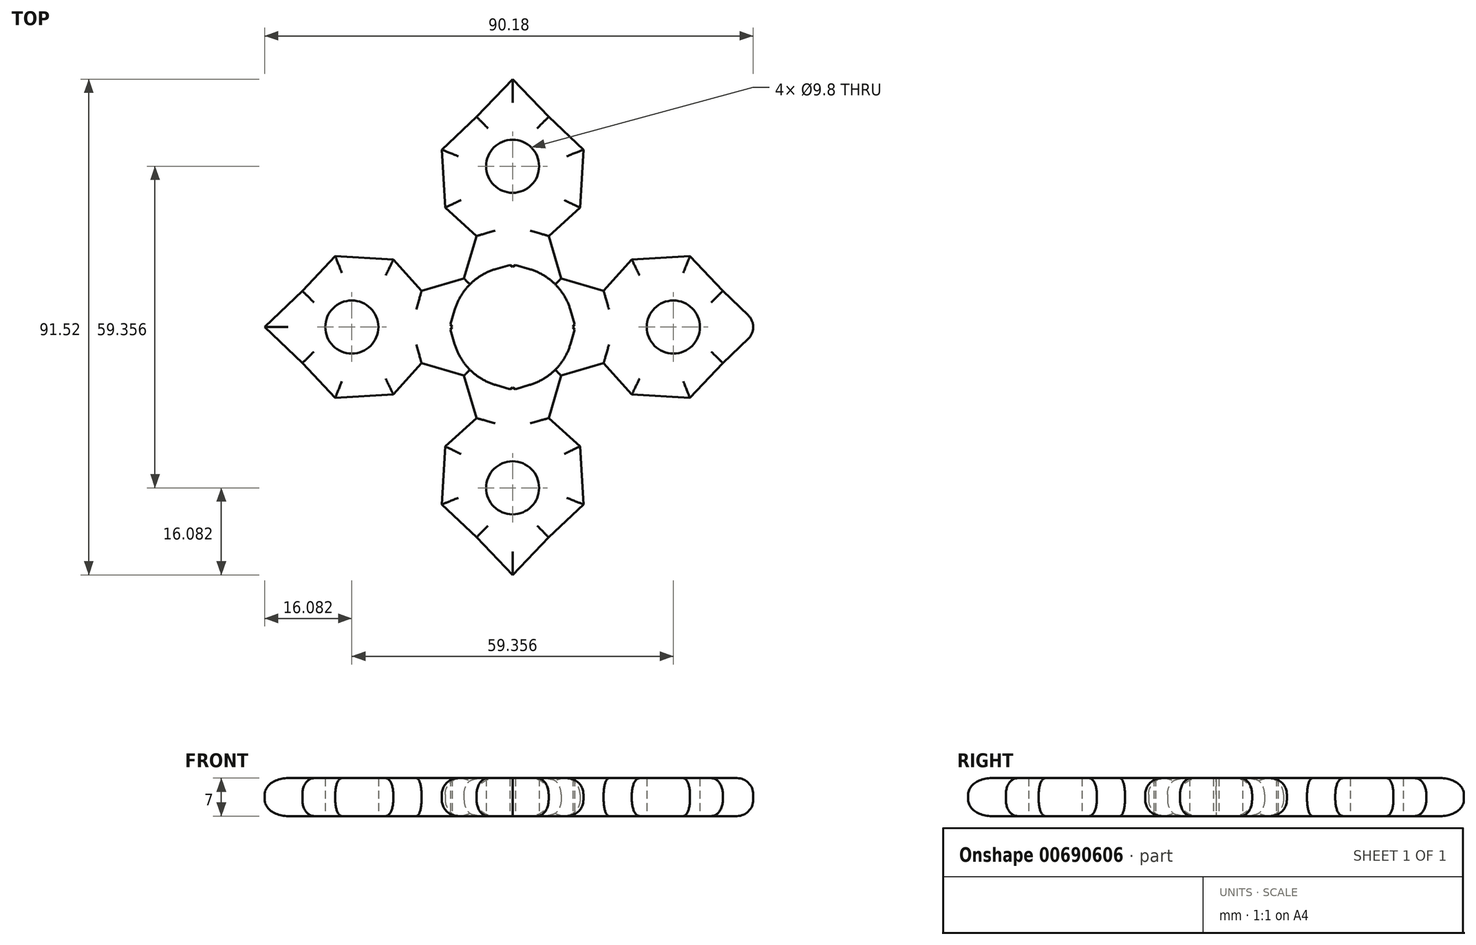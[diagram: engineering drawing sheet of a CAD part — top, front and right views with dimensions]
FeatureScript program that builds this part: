
annotation { "Feature Type Name" : "Feature", "Feature Type Description" : "" }
export const myFeature = defineFeature(function(context is Context, id is Id, definition is map)
    precondition{}
    {
        {
            var Q0;
            Q0=qCreatedBy(makeId("Top.planeOp"),FACE);
            var sketch = newSketch(context, id + "F0", { "sketchPlane" : qUnion([Q0])});
            skCircle(sketch, "E0", {"center": v(0, 0) * mm, "radius": 11.14 * mm});
            skCircle(sketch, "E1", {"center": v(29.68, 0) * mm, "radius": 4.9 * mm});
            skLineSegment(sketch, "E2", {"start": v(0, 11.14) * mm, "end": v(0.51, 11.46) * mm});
            skLineSegment(sketch, "E3", {"start": v(0.51, 11.46) * mm, "end": v(16.8, 6.66) * mm});
            skLineSegment(sketch, "E4", {"start": v(16.8, 6.66) * mm, "end": v(22.02, 12.45) * mm});
            skLineSegment(sketch, "E5", {"start": v(22.02, 12.45) * mm, "end": v(32.74, 13.08) * mm});
            skLineSegment(sketch, "E6", {"start": v(32.74, 13.08) * mm, "end": v(38.81, 6.66) * mm});
            skLineSegment(sketch, "E7", {"start": v(38.81, 6.66) * mm, "end": v(45.76, 0) * mm});
            skLineSegment(sketch, "E8.MirrorCS", {"start": v(0.51, -11.46) * mm, "end": v(16.8, -6.66) * mm});
            skLineSegment(sketch, "E9.MirrorCS", {"start": v(0, -11.14) * mm, "end": v(0.51, -11.46) * mm});
            skLineSegment(sketch, "E10.MirrorCS", {"start": v(16.8, -6.66) * mm, "end": v(22.02, -12.45) * mm});
            skLineSegment(sketch, "E11.MirrorCS", {"start": v(22.02, -12.45) * mm, "end": v(32.74, -13.08) * mm});
            skLineSegment(sketch, "E12.MirrorCS", {"start": v(32.74, -13.08) * mm, "end": v(38.81, -6.66) * mm});
            skLineSegment(sketch, "E13.MirrorCS", {"start": v(38.81, -6.66) * mm, "end": v(45.76, 0) * mm});
            skLineSegment(sketch, "E14.1.0", {"start": v(-12.45, 22.02) * mm, "end": v(-13.08, 32.74) * mm});
            skLineSegment(sketch, "E14.1.1", {"start": v(-13.08, 32.74) * mm, "end": v(-6.66, 38.81) * mm});
            skLineSegment(sketch, "E14.1.2", {"start": v(11.46, 0.51) * mm, "end": v(6.66, 16.8) * mm});
            skLineSegment(sketch, "E14.1.3", {"start": v(-6.66, 38.81) * mm, "end": v(0, 45.76) * mm});
            skLineSegment(sketch, "E14.1.4", {"start": v(11.14, 0) * mm, "end": v(11.46, 0.51) * mm});
            skLineSegment(sketch, "E14.1.5", {"start": v(-6.66, 16.8) * mm, "end": v(-12.45, 22.02) * mm});
            skLineSegment(sketch, "E14.1.6", {"start": v(6.66, 16.8) * mm, "end": v(12.45, 22.02) * mm});
            skLineSegment(sketch, "E14.1.7", {"start": v(-11.46, 0.51) * mm, "end": v(-6.66, 16.8) * mm});
            skLineSegment(sketch, "E14.1.8", {"start": v(12.45, 22.02) * mm, "end": v(13.08, 32.74) * mm});
            skLineSegment(sketch, "E14.1.9", {"start": v(13.08, 32.74) * mm, "end": v(6.66, 38.81) * mm});
            skLineSegment(sketch, "E14.1.10", {"start": v(-11.14, 0) * mm, "end": v(-11.46, 0.51) * mm});
            skLineSegment(sketch, "E14.1.11", {"start": v(6.66, 38.81) * mm, "end": v(0, 45.76) * mm});
            skCircle(sketch, "E14.1.12", {"center": v(0, 29.68) * mm, "radius": 4.9 * mm});
            skLineSegment(sketch, "E14.2.0", {"start": v(-22.02, -12.45) * mm, "end": v(-32.74, -13.08) * mm});
            skLineSegment(sketch, "E14.2.1", {"start": v(-32.74, -13.08) * mm, "end": v(-38.81, -6.66) * mm});
            skLineSegment(sketch, "E14.2.2", {"start": v(-0.51, 11.46) * mm, "end": v(-16.8, 6.66) * mm});
            skLineSegment(sketch, "E14.2.3", {"start": v(-38.81, -6.66) * mm, "end": v(-45.76, 0) * mm});
            skLineSegment(sketch, "E14.2.4", {"start": v(0, 11.14) * mm, "end": v(-0.51, 11.46) * mm});
            skLineSegment(sketch, "E14.2.5", {"start": v(-16.8, -6.66) * mm, "end": v(-22.02, -12.45) * mm});
            skLineSegment(sketch, "E14.2.6", {"start": v(-16.8, 6.66) * mm, "end": v(-22.02, 12.45) * mm});
            skLineSegment(sketch, "E14.2.7", {"start": v(-0.51, -11.46) * mm, "end": v(-16.8, -6.66) * mm});
            skLineSegment(sketch, "E14.2.8", {"start": v(-22.02, 12.45) * mm, "end": v(-32.74, 13.08) * mm});
            skLineSegment(sketch, "E14.2.9", {"start": v(-32.74, 13.08) * mm, "end": v(-38.81, 6.66) * mm});
            skLineSegment(sketch, "E14.2.10", {"start": v(0, -11.14) * mm, "end": v(-0.51, -11.46) * mm});
            skLineSegment(sketch, "E14.2.11", {"start": v(-38.81, 6.66) * mm, "end": v(-45.76, 0) * mm});
            skCircle(sketch, "E14.2.12", {"center": v(-29.68, 0) * mm, "radius": 4.9 * mm});
            skLineSegment(sketch, "E14.3.0", {"start": v(12.45, -22.02) * mm, "end": v(13.08, -32.74) * mm});
            skLineSegment(sketch, "E14.3.1", {"start": v(13.08, -32.74) * mm, "end": v(6.66, -38.81) * mm});
            skLineSegment(sketch, "E14.3.2", {"start": v(-11.46, -0.51) * mm, "end": v(-6.66, -16.8) * mm});
            skLineSegment(sketch, "E14.3.3", {"start": v(6.66, -38.81) * mm, "end": v(0, -45.76) * mm});
            skLineSegment(sketch, "E14.3.4", {"start": v(-11.14, 0) * mm, "end": v(-11.46, -0.51) * mm});
            skLineSegment(sketch, "E14.3.5", {"start": v(6.66, -16.8) * mm, "end": v(12.45, -22.02) * mm});
            skLineSegment(sketch, "E14.3.6", {"start": v(-6.66, -16.8) * mm, "end": v(-12.45, -22.02) * mm});
            skLineSegment(sketch, "E14.3.7", {"start": v(11.46, -0.51) * mm, "end": v(6.66, -16.8) * mm});
            skLineSegment(sketch, "E14.3.8", {"start": v(-12.45, -22.02) * mm, "end": v(-13.08, -32.74) * mm});
            skLineSegment(sketch, "E14.3.9", {"start": v(-13.08, -32.74) * mm, "end": v(-6.66, -38.81) * mm});
            skLineSegment(sketch, "E14.3.10", {"start": v(11.14, 0) * mm, "end": v(11.46, -0.51) * mm});
            skLineSegment(sketch, "E14.3.11", {"start": v(-6.66, -38.81) * mm, "end": v(0, -45.76) * mm});
            skCircle(sketch, "E14.3.12", {"center": v(0, -29.68) * mm, "radius": 4.9 * mm});
            skSolve(sketch);
        }
        {
            var Q0;
            Q0 = qSketchRegion(id + "F0", true);
            extrude(context, id + "F1", {"entities" : qUnion([Q0]), "depth" : 7 * mm, "offsetDistance" : 25 * mm});
        }
        {
            var Q0;
            Q0=makeQuery(id+"F1.opExtrude","SWEPT_EDGE",EDGE,{"disambiguationData":[OSD([sQuery(id+"F0.wireOp",EDGE,"E7"),sQuery(id+"F0.wireOp",EDGE,"E13.MirrorCS")])]});
            var Q1;
            Q1=makeQuery(id+"F1.opExtrude","CAP_EDGE",EDGE,{"disambiguationData":[OSD([sQuery(id+"F0.wireOp",EDGE,"E14.1.11")])],"isStart":false});
            var Q2;
            Q2=makeQuery(id+"F1.opExtrude","CAP_EDGE",EDGE,{"disambiguationData":[OSD([sQuery(id+"F0.wireOp",EDGE,"E14.1.8")])],"isStart":false});
            var Q3;
            Q3=makeQuery(id+"F1.opExtrude","CAP_EDGE",EDGE,{"disambiguationData":[OSD([sQuery(id+"F0.wireOp",EDGE,"E14.1.6")])],"isStart":false});
            var Q4;
            {var subQ0=sQuery(id+"F0.wireOp",EDGE,"E14.1.2");Q4=makeQuery(id+"F1.opExtrude","CAP_EDGE",EDGE,{"disambiguationData":[OSD([subQ0]),TDD([makeQuery(id+"F0.imprint","IMPRINT",EDGE,{"disambiguationData":[TD([[makeQuery(id+"F0.imprint","INTERSECT",VERTEX,{"derivedFrom":[subQ0,sQuery(id+"F0.wireOp",EDGE,"E14.1.6")]}),1.0]])],"derivedFrom":subQ0})])],"isStart":false});}
            var Q5;
            {var subQ0=sQuery(id+"F0.wireOp",EDGE,"E3");Q5=makeQuery(id+"F1.opExtrude","CAP_EDGE",EDGE,{"disambiguationData":[OSD([subQ0]),TDD([makeQuery(id+"F0.imprint","IMPRINT",EDGE,{"disambiguationData":[TD([[makeQuery(id+"F0.imprint","INTERSECT",VERTEX,{"derivedFrom":[subQ0,sQuery(id+"F0.wireOp",EDGE,"E4")]}),1.0]])],"derivedFrom":subQ0})])],"isStart":false});}
            var Q6;
            Q6=makeQuery(id+"F1.opExtrude","CAP_EDGE",EDGE,{"disambiguationData":[OSD([sQuery(id+"F0.wireOp",EDGE,"E4")])],"isStart":false});
            var Q7;
            Q7=makeQuery(id+"F1.opExtrude","CAP_EDGE",EDGE,{"disambiguationData":[OSD([sQuery(id+"F0.wireOp",EDGE,"E5")])],"isStart":false});
            var Q8;
            Q8=makeQuery(id+"F1.opExtrude","CAP_EDGE",EDGE,{"disambiguationData":[OSD([sQuery(id+"F0.wireOp",EDGE,"E6")])],"isStart":false});
            var Q9;
            Q9=makeQuery(id+"F1.opExtrude","CAP_EDGE",EDGE,{"disambiguationData":[OSD([sQuery(id+"F0.wireOp",EDGE,"E13.MirrorCS")])],"isStart":false});
            var Q10;
            Q10=makeQuery(id+"F1.opExtrude","CAP_EDGE",EDGE,{"disambiguationData":[OSD([sQuery(id+"F0.wireOp",EDGE,"E12.MirrorCS")])],"isStart":false});
            var Q11;
            Q11=makeQuery(id+"F1.opExtrude","CAP_EDGE",EDGE,{"disambiguationData":[OSD([sQuery(id+"F0.wireOp",EDGE,"E11.MirrorCS")])],"isStart":false});
            var Q12;
            Q12=makeQuery(id+"F1.opExtrude","CAP_EDGE",EDGE,{"disambiguationData":[OSD([sQuery(id+"F0.wireOp",EDGE,"E10.MirrorCS")])],"isStart":false});
            var Q13;
            {var subQ0=sQuery(id+"F0.wireOp",EDGE,"E8.MirrorCS");Q13=makeQuery(id+"F1.opExtrude","CAP_EDGE",EDGE,{"disambiguationData":[OSD([subQ0]),TDD([makeQuery(id+"F0.imprint","IMPRINT",EDGE,{"disambiguationData":[TD([[makeQuery(id+"F0.imprint","INTERSECT",VERTEX,{"derivedFrom":[subQ0,sQuery(id+"F0.wireOp",EDGE,"E10.MirrorCS")]}),1.0]])],"derivedFrom":subQ0})])],"isStart":false});}
            var Q14;
            {var subQ0=sQuery(id+"F0.wireOp",EDGE,"E14.3.7");Q14=makeQuery(id+"F1.opExtrude","CAP_EDGE",EDGE,{"disambiguationData":[OSD([subQ0]),TDD([makeQuery(id+"F0.imprint","IMPRINT",EDGE,{"disambiguationData":[TD([[makeQuery(id+"F0.imprint","INTERSECT",VERTEX,{"derivedFrom":[sQuery(id+"F0.wireOp",EDGE,"E14.3.5"),subQ0]}),1.0]])],"derivedFrom":subQ0})])],"isStart":false});}
            var Q15;
            Q15=makeQuery(id+"F1.opExtrude","CAP_EDGE",EDGE,{"disambiguationData":[OSD([sQuery(id+"F0.wireOp",EDGE,"E14.3.5")])],"isStart":false});
            var Q16;
            Q16=makeQuery(id+"F1.opExtrude","CAP_EDGE",EDGE,{"disambiguationData":[OSD([sQuery(id+"F0.wireOp",EDGE,"E14.3.0")])],"isStart":false});
            var Q17;
            Q17=makeQuery(id+"F1.opExtrude","CAP_EDGE",EDGE,{"disambiguationData":[OSD([sQuery(id+"F0.wireOp",EDGE,"E14.3.3")])],"isStart":false});
            var Q18;
            Q18=makeQuery(id+"F1.opExtrude","CAP_EDGE",EDGE,{"disambiguationData":[OSD([sQuery(id+"F0.wireOp",EDGE,"E14.3.1")])],"isStart":false});
            var Q19;
            Q19=makeQuery(id+"F1.opExtrude","CAP_EDGE",EDGE,{"disambiguationData":[OSD([sQuery(id+"F0.wireOp",EDGE,"E14.1.9")])],"isStart":false});
            var Q20;
            Q20=makeQuery(id+"F1.opExtrude","CAP_EDGE",EDGE,{"disambiguationData":[OSD([sQuery(id+"F0.wireOp",EDGE,"E14.3.11")])],"isStart":false});
            var Q21;
            Q21=makeQuery(id+"F1.opExtrude","CAP_EDGE",EDGE,{"disambiguationData":[OSD([sQuery(id+"F0.wireOp",EDGE,"E14.3.9")])],"isStart":false});
            var Q22;
            Q22=makeQuery(id+"F1.opExtrude","CAP_EDGE",EDGE,{"disambiguationData":[OSD([sQuery(id+"F0.wireOp",EDGE,"E14.3.6")])],"isStart":false});
            var Q23;
            Q23=makeQuery(id+"F1.opExtrude","CAP_EDGE",EDGE,{"disambiguationData":[OSD([sQuery(id+"F0.wireOp",EDGE,"E14.3.8")])],"isStart":false});
            var Q24;
            {var subQ0=sQuery(id+"F0.wireOp",EDGE,"E14.3.2");Q24=makeQuery(id+"F1.opExtrude","CAP_EDGE",EDGE,{"disambiguationData":[OSD([subQ0]),TDD([makeQuery(id+"F0.imprint","IMPRINT",EDGE,{"disambiguationData":[TD([[makeQuery(id+"F0.imprint","INTERSECT",VERTEX,{"derivedFrom":[subQ0,sQuery(id+"F0.wireOp",EDGE,"E14.3.6")]}),1.0]])],"derivedFrom":subQ0})])],"isStart":false});}
            var Q25;
            {var subQ0=sQuery(id+"F0.wireOp",EDGE,"E14.2.7");Q25=makeQuery(id+"F1.opExtrude","CAP_EDGE",EDGE,{"disambiguationData":[OSD([subQ0]),TDD([makeQuery(id+"F0.imprint","IMPRINT",EDGE,{"disambiguationData":[TD([[makeQuery(id+"F0.imprint","INTERSECT",VERTEX,{"derivedFrom":[sQuery(id+"F0.wireOp",EDGE,"E14.2.5"),subQ0]}),1.0]])],"derivedFrom":subQ0})])],"isStart":false});}
            var Q26;
            Q26=makeQuery(id+"F1.opExtrude","CAP_EDGE",EDGE,{"disambiguationData":[OSD([sQuery(id+"F0.wireOp",EDGE,"E14.2.5")])],"isStart":false});
            var Q27;
            Q27=makeQuery(id+"F1.opExtrude","CAP_EDGE",EDGE,{"disambiguationData":[OSD([sQuery(id+"F0.wireOp",EDGE,"E14.2.0")])],"isStart":false});
            var Q28;
            Q28=makeQuery(id+"F1.opExtrude","CAP_EDGE",EDGE,{"disambiguationData":[OSD([sQuery(id+"F0.wireOp",EDGE,"E14.2.1")])],"isStart":false});
            var Q29;
            Q29=makeQuery(id+"F1.opExtrude","CAP_EDGE",EDGE,{"disambiguationData":[OSD([sQuery(id+"F0.wireOp",EDGE,"E14.2.3")])],"isStart":false});
            var Q30;
            {var subQ0=sQuery(id+"F0.wireOp",EDGE,"E14.2.2");Q30=makeQuery(id+"F1.opExtrude","CAP_EDGE",EDGE,{"disambiguationData":[OSD([subQ0]),TDD([makeQuery(id+"F0.imprint","IMPRINT",EDGE,{"disambiguationData":[TD([[makeQuery(id+"F0.imprint","INTERSECT",VERTEX,{"derivedFrom":[subQ0,sQuery(id+"F0.wireOp",EDGE,"E14.2.6")]}),1.0]])],"derivedFrom":subQ0})])],"isStart":false});}
            var Q31;
            Q31=makeQuery(id+"F1.opExtrude","CAP_EDGE",EDGE,{"disambiguationData":[OSD([sQuery(id+"F0.wireOp",EDGE,"E14.2.6")])],"isStart":false});
            var Q32;
            Q32=makeQuery(id+"F1.opExtrude","CAP_EDGE",EDGE,{"disambiguationData":[OSD([sQuery(id+"F0.wireOp",EDGE,"E14.2.8")])],"isStart":false});
            var Q33;
            Q33=makeQuery(id+"F1.opExtrude","CAP_EDGE",EDGE,{"disambiguationData":[OSD([sQuery(id+"F0.wireOp",EDGE,"E14.2.11")])],"isStart":false});
            var Q34;
            Q34=makeQuery(id+"F1.opExtrude","CAP_EDGE",EDGE,{"disambiguationData":[OSD([sQuery(id+"F0.wireOp",EDGE,"E14.2.9")])],"isStart":false});
            var Q35;
            {var subQ0=sQuery(id+"F0.wireOp",EDGE,"E14.1.7");Q35=makeQuery(id+"F1.opExtrude","CAP_EDGE",EDGE,{"disambiguationData":[OSD([subQ0]),TDD([makeQuery(id+"F0.imprint","IMPRINT",EDGE,{"disambiguationData":[TD([[makeQuery(id+"F0.imprint","INTERSECT",VERTEX,{"derivedFrom":[sQuery(id+"F0.wireOp",EDGE,"E14.1.5"),subQ0]}),1.0]])],"derivedFrom":subQ0})])],"isStart":false});}
            var Q36;
            Q36=makeQuery(id+"F1.opExtrude","CAP_EDGE",EDGE,{"disambiguationData":[OSD([sQuery(id+"F0.wireOp",EDGE,"E14.1.5")])],"isStart":false});
            var Q37;
            Q37=makeQuery(id+"F1.opExtrude","CAP_EDGE",EDGE,{"disambiguationData":[OSD([sQuery(id+"F0.wireOp",EDGE,"E14.1.0")])],"isStart":false});
            var Q38;
            Q38=makeQuery(id+"F1.opExtrude","CAP_EDGE",EDGE,{"disambiguationData":[OSD([sQuery(id+"F0.wireOp",EDGE,"E14.1.1")])],"isStart":false});
            var Q39;
            Q39=makeQuery(id+"F1.opExtrude","CAP_EDGE",EDGE,{"disambiguationData":[OSD([sQuery(id+"F0.wireOp",EDGE,"E14.1.3")])],"isStart":false});
            var Q40;
            Q40=makeQuery(id+"F1.opExtrude","CAP_EDGE",EDGE,{"disambiguationData":[OSD([sQuery(id+"F0.wireOp",EDGE,"E7")])],"isStart":true});
            var Q41;
            Q41=makeQuery(id+"F1.opExtrude","CAP_EDGE",EDGE,{"disambiguationData":[OSD([sQuery(id+"F0.wireOp",EDGE,"E6")])],"isStart":true});
            var Q42;
            Q42=makeQuery(id+"F1.opExtrude","CAP_EDGE",EDGE,{"disambiguationData":[OSD([sQuery(id+"F0.wireOp",EDGE,"E5")])],"isStart":true});
            var Q43;
            Q43=makeQuery(id+"F1.opExtrude","CAP_EDGE",EDGE,{"disambiguationData":[OSD([sQuery(id+"F0.wireOp",EDGE,"E4")])],"isStart":true});
            var Q44;
            {var subQ0=sQuery(id+"F0.wireOp",EDGE,"E3");Q44=makeQuery(id+"F1.opExtrude","CAP_EDGE",EDGE,{"disambiguationData":[OSD([subQ0]),TDD([makeQuery(id+"F0.imprint","IMPRINT",EDGE,{"disambiguationData":[TD([[makeQuery(id+"F0.imprint","INTERSECT",VERTEX,{"derivedFrom":[subQ0,sQuery(id+"F0.wireOp",EDGE,"E4")]}),1.0]])],"derivedFrom":subQ0})])],"isStart":true});}
            var Q45;
            {var subQ0=sQuery(id+"F0.wireOp",EDGE,"E14.1.2");Q45=makeQuery(id+"F1.opExtrude","CAP_EDGE",EDGE,{"disambiguationData":[OSD([subQ0]),TDD([makeQuery(id+"F0.imprint","IMPRINT",EDGE,{"disambiguationData":[TD([[makeQuery(id+"F0.imprint","INTERSECT",VERTEX,{"derivedFrom":[subQ0,sQuery(id+"F0.wireOp",EDGE,"E14.1.6")]}),1.0]])],"derivedFrom":subQ0})])],"isStart":true});}
            var Q46;
            Q46=makeQuery(id+"F1.opExtrude","CAP_EDGE",EDGE,{"disambiguationData":[OSD([sQuery(id+"F0.wireOp",EDGE,"E14.1.6")])],"isStart":true});
            var Q47;
            Q47=makeQuery(id+"F1.opExtrude","CAP_EDGE",EDGE,{"disambiguationData":[OSD([sQuery(id+"F0.wireOp",EDGE,"E14.1.8")])],"isStart":true});
            var Q48;
            Q48=makeQuery(id+"F1.opExtrude","CAP_EDGE",EDGE,{"disambiguationData":[OSD([sQuery(id+"F0.wireOp",EDGE,"E14.1.9")])],"isStart":true});
            var Q49;
            Q49=makeQuery(id+"F1.opExtrude","CAP_EDGE",EDGE,{"disambiguationData":[OSD([sQuery(id+"F0.wireOp",EDGE,"E14.1.11")])],"isStart":true});
            var Q50;
            {var subQ0=sQuery(id+"F0.wireOp",EDGE,"E14.1.7");Q50=makeQuery(id+"F1.opExtrude","CAP_EDGE",EDGE,{"disambiguationData":[OSD([subQ0]),TDD([makeQuery(id+"F0.imprint","IMPRINT",EDGE,{"disambiguationData":[TD([[makeQuery(id+"F0.imprint","INTERSECT",VERTEX,{"derivedFrom":[sQuery(id+"F0.wireOp",EDGE,"E14.1.5"),subQ0]}),1.0]])],"derivedFrom":subQ0})])],"isStart":true});}
            var Q51;
            Q51=makeQuery(id+"F1.opExtrude","CAP_EDGE",EDGE,{"disambiguationData":[OSD([sQuery(id+"F0.wireOp",EDGE,"E14.1.3")])],"isStart":true});
            var Q52;
            Q52=makeQuery(id+"F1.opExtrude","CAP_EDGE",EDGE,{"disambiguationData":[OSD([sQuery(id+"F0.wireOp",EDGE,"E14.1.1")])],"isStart":true});
            var Q53;
            Q53=makeQuery(id+"F1.opExtrude","CAP_EDGE",EDGE,{"disambiguationData":[OSD([sQuery(id+"F0.wireOp",EDGE,"E14.1.5")])],"isStart":true});
            var Q54;
            Q54=makeQuery(id+"F1.opExtrude","CAP_EDGE",EDGE,{"disambiguationData":[OSD([sQuery(id+"F0.wireOp",EDGE,"E14.1.0")])],"isStart":true});
            var Q55;
            {var subQ0=sQuery(id+"F0.wireOp",EDGE,"E14.2.2");Q55=makeQuery(id+"F1.opExtrude","CAP_EDGE",EDGE,{"disambiguationData":[OSD([subQ0]),TDD([makeQuery(id+"F0.imprint","IMPRINT",EDGE,{"disambiguationData":[TD([[makeQuery(id+"F0.imprint","INTERSECT",VERTEX,{"derivedFrom":[subQ0,sQuery(id+"F0.wireOp",EDGE,"E14.2.6")]}),1.0]])],"derivedFrom":subQ0})])],"isStart":true});}
            var Q56;
            Q56=makeQuery(id+"F1.opExtrude","CAP_EDGE",EDGE,{"disambiguationData":[OSD([sQuery(id+"F0.wireOp",EDGE,"E14.2.6")])],"isStart":true});
            var Q57;
            {var subQ0=sQuery(id+"F0.wireOp",EDGE,"E14.2.7");Q57=makeQuery(id+"F1.opExtrude","CAP_EDGE",EDGE,{"disambiguationData":[OSD([subQ0]),TDD([makeQuery(id+"F0.imprint","IMPRINT",EDGE,{"disambiguationData":[TD([[makeQuery(id+"F0.imprint","INTERSECT",VERTEX,{"derivedFrom":[sQuery(id+"F0.wireOp",EDGE,"E14.2.5"),subQ0]}),1.0]])],"derivedFrom":subQ0})])],"isStart":true});}
            var Q58;
            Q58=makeQuery(id+"F1.opExtrude","CAP_EDGE",EDGE,{"disambiguationData":[OSD([sQuery(id+"F0.wireOp",EDGE,"E14.2.8")])],"isStart":true});
            var Q59;
            Q59=makeQuery(id+"F1.opExtrude","CAP_EDGE",EDGE,{"disambiguationData":[OSD([sQuery(id+"F0.wireOp",EDGE,"E14.2.5")])],"isStart":true});
            var Q60;
            Q60=makeQuery(id+"F1.opExtrude","CAP_EDGE",EDGE,{"disambiguationData":[OSD([sQuery(id+"F0.wireOp",EDGE,"E14.2.1")])],"isStart":true});
            var Q61;
            Q61=makeQuery(id+"F1.opExtrude","CAP_EDGE",EDGE,{"disambiguationData":[OSD([sQuery(id+"F0.wireOp",EDGE,"E14.2.0")])],"isStart":true});
            var Q62;
            Q62=makeQuery(id+"F1.opExtrude","CAP_EDGE",EDGE,{"disambiguationData":[OSD([sQuery(id+"F0.wireOp",EDGE,"E14.2.9")])],"isStart":true});
            var Q63;
            Q63=makeQuery(id+"F1.opExtrude","CAP_EDGE",EDGE,{"disambiguationData":[OSD([sQuery(id+"F0.wireOp",EDGE,"E14.2.11")])],"isStart":true});
            var Q64;
            {var subQ0=sQuery(id+"F0.wireOp",EDGE,"E14.3.2");Q64=makeQuery(id+"F1.opExtrude","CAP_EDGE",EDGE,{"disambiguationData":[OSD([subQ0]),TDD([makeQuery(id+"F0.imprint","IMPRINT",EDGE,{"disambiguationData":[TD([[makeQuery(id+"F0.imprint","INTERSECT",VERTEX,{"derivedFrom":[subQ0,sQuery(id+"F0.wireOp",EDGE,"E14.3.6")]}),1.0]])],"derivedFrom":subQ0})])],"isStart":true});}
            var Q65;
            Q65=makeQuery(id+"F1.opExtrude","CAP_EDGE",EDGE,{"disambiguationData":[OSD([sQuery(id+"F0.wireOp",EDGE,"E14.3.6")])],"isStart":true});
            var Q66;
            Q66=makeQuery(id+"F1.opExtrude","CAP_EDGE",EDGE,{"disambiguationData":[OSD([sQuery(id+"F0.wireOp",EDGE,"E14.3.8")])],"isStart":true});
            var Q67;
            Q67=makeQuery(id+"F1.opExtrude","CAP_EDGE",EDGE,{"disambiguationData":[OSD([sQuery(id+"F0.wireOp",EDGE,"E14.3.9")])],"isStart":true});
            var Q68;
            Q68=makeQuery(id+"F1.opExtrude","CAP_EDGE",EDGE,{"disambiguationData":[OSD([sQuery(id+"F0.wireOp",EDGE,"E14.3.11")])],"isStart":true});
            var Q69;
            {var subQ0=sQuery(id+"F0.wireOp",EDGE,"E14.3.7");Q69=makeQuery(id+"F1.opExtrude","CAP_EDGE",EDGE,{"disambiguationData":[OSD([subQ0]),TDD([makeQuery(id+"F0.imprint","IMPRINT",EDGE,{"disambiguationData":[TD([[makeQuery(id+"F0.imprint","INTERSECT",VERTEX,{"derivedFrom":[sQuery(id+"F0.wireOp",EDGE,"E14.3.5"),subQ0]}),1.0]])],"derivedFrom":subQ0})])],"isStart":true});}
            var Q70;
            Q70=makeQuery(id+"F1.opExtrude","CAP_EDGE",EDGE,{"disambiguationData":[OSD([sQuery(id+"F0.wireOp",EDGE,"E14.3.3")])],"isStart":true});
            var Q71;
            Q71=makeQuery(id+"F1.opExtrude","CAP_EDGE",EDGE,{"disambiguationData":[OSD([sQuery(id+"F0.wireOp",EDGE,"E14.3.1")])],"isStart":true});
            var Q72;
            Q72=makeQuery(id+"F1.opExtrude","CAP_EDGE",EDGE,{"disambiguationData":[OSD([sQuery(id+"F0.wireOp",EDGE,"E14.3.0")])],"isStart":true});
            var Q73;
            Q73=makeQuery(id+"F1.opExtrude","CAP_EDGE",EDGE,{"disambiguationData":[OSD([sQuery(id+"F0.wireOp",EDGE,"E14.3.5")])],"isStart":true});
            var Q74;
            {var subQ0=sQuery(id+"F0.wireOp",EDGE,"E8.MirrorCS");Q74=makeQuery(id+"F1.opExtrude","CAP_EDGE",EDGE,{"disambiguationData":[OSD([subQ0]),TDD([makeQuery(id+"F0.imprint","IMPRINT",EDGE,{"disambiguationData":[TD([[makeQuery(id+"F0.imprint","INTERSECT",VERTEX,{"derivedFrom":[subQ0,sQuery(id+"F0.wireOp",EDGE,"E10.MirrorCS")]}),1.0]])],"derivedFrom":subQ0})])],"isStart":true});}
            var Q75;
            Q75=makeQuery(id+"F1.opExtrude","CAP_EDGE",EDGE,{"disambiguationData":[OSD([sQuery(id+"F0.wireOp",EDGE,"E10.MirrorCS")])],"isStart":true});
            var Q76;
            Q76=makeQuery(id+"F1.opExtrude","CAP_EDGE",EDGE,{"disambiguationData":[OSD([sQuery(id+"F0.wireOp",EDGE,"E13.MirrorCS")])],"isStart":true});
            var Q77;
            Q77=makeQuery(id+"F1.opExtrude","CAP_EDGE",EDGE,{"disambiguationData":[OSD([sQuery(id+"F0.wireOp",EDGE,"E11.MirrorCS")])],"isStart":true});
            fillet(context, id + "F2", {"entities" : qUnion([Q0, Q1, Q2, Q3, Q4, Q5, Q6, Q7, Q8, Q9, Q10, Q11, Q12, Q13, Q14, Q15, Q16, Q17, Q18, Q19, Q20, Q21, Q22, Q23, Q24, Q25, Q26, Q27, Q28, Q29, Q30, Q31, Q32, Q33, Q34, Q35, Q36, Q37, Q38, Q39, Q40, Q41, Q42, Q43, Q44, Q45, Q46, Q47, Q48, Q49, Q50, Q51, Q52, Q53, Q54, Q55, Q56, Q57, Q58, Q59, Q60, Q61, Q62, Q63, Q64, Q65, Q66, Q67, Q68, Q69, Q70, Q71, Q72, Q73, Q74, Q75, Q76, Q77]), "radius" : 3 * mm, "tangentPropagation" : true, "allowEdgeOverflow" : false});
        }
    });
